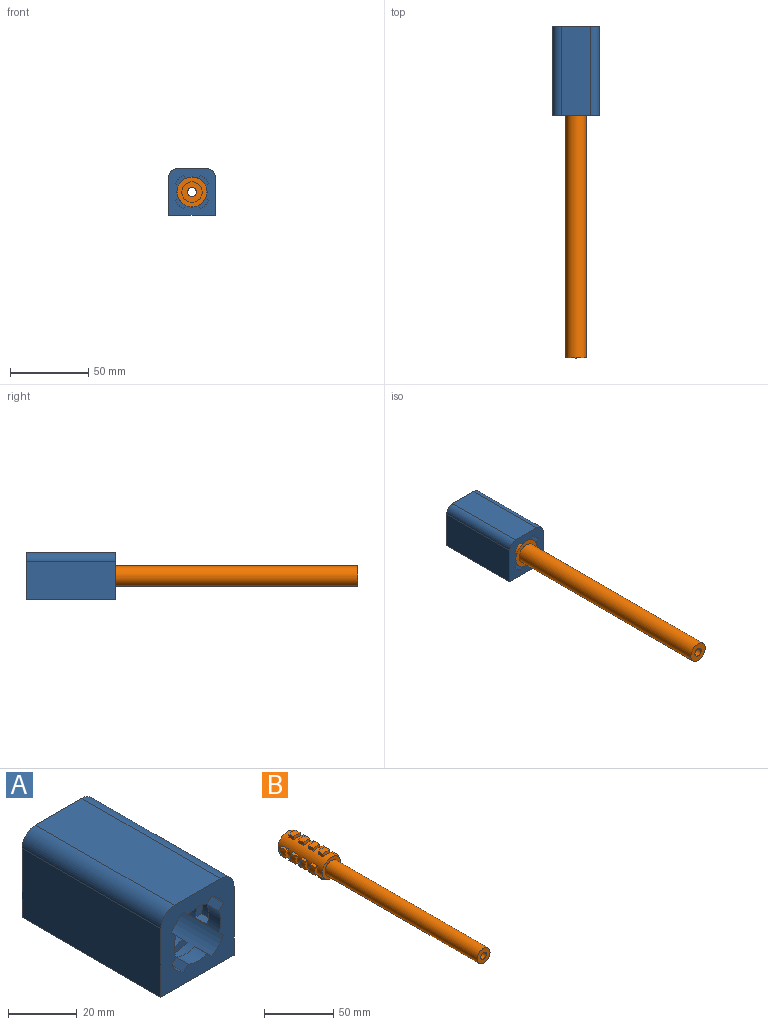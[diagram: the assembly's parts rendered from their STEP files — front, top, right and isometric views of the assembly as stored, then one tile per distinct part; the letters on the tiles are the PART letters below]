
ASSEMBLY  parts=2 mates=1
PART A: 121 faces, bbox 30x57x30 mm
  f0: plane 30x30mm, normal (0,1,0), area 631mm2, adj f33,f34,f35,f36,f37,f42,f43,f95
  f1: plane 4.88x4.88mm, normal (0,-1,0), area 12.5mm2, adj f37,f96,f109,f117
  f2: plane 5.27x3.17mm, normal (0,-1,0), area 12.5mm2, adj f37,f107,f110,f116
  f3: plane 4.88x4.88mm, normal (0,-1,0), area 12.5mm2, adj f37,f105,f108,f115
  f4: plane 5.27x3.17mm, normal (0,-1,0), area 12.5mm2, adj f37,f103,f106,f114
  f5: plane 4.88x4.88mm, normal (0,-1,0), area 12.5mm2, adj f37,f102,f104,f113
  f6: plane 5.27x3.17mm, normal (0,-1,0), area 12.5mm2, adj f37,f99,f101,f112
  f7: plane 4.88x4.88mm, normal (0,-1,0), area 12.5mm2, adj f37,f97,f100,f111
  f8: plane 5.27x3.17mm, normal (0,-1,0), area 12.5mm2, adj f37,f95,f98,f118
  f9: cylinder r=12.1mm len=40mm, axis (0,1,0), area 474.1mm2, adj f10,f17,f21,f25,f30,f47,f50,f60
  f10: plane 5x2.64mm, normal (0,0,-1), area 13.2mm2, adj f9,f37,f84,f93
  f11: cylinder r=12.1mm len=40mm, axis (0,1,0), area 474.1mm2, adj f12,f18,f22,f26,f31,f48,f50,f57
  f12: plane 5x2.64mm, normal (-1,0,0), area 13.2mm2, adj f11,f37,f81,f91
  f13: cylinder r=12.1mm len=40mm, axis (0,1,0), area 474.1mm2, adj f14,f19,f23,f27,f32,f49,f50,f54
  f14: plane 5x2.64mm, normal (0,0,1), area 13.2mm2, adj f13,f37,f79,f89
  f15: cylinder r=12.1mm len=40mm, axis (0,1,0), area 474.1mm2, adj f16,f20,f24,f28,f29,f46,f50,f51
  f16: plane 5x2.64mm, normal (1,0,0), area 13.2mm2, adj f15,f37,f75,f87
  f17: plane 5x2.64mm, normal (0,0,-1), area 13.2mm2, adj f9,f37,f72,f85
  f18: plane 5x2.64mm, normal (-1,0,0), area 13.2mm2, adj f11,f37,f69,f82
  f19: plane 5x2.64mm, normal (0,0,1), area 13.2mm2, adj f13,f37,f66,f80
  f20: plane 5x2.64mm, normal (1,0,0), area 13.2mm2, adj f15,f37,f63,f76
  f21: plane 5x2.64mm, normal (0,0,-1), area 13.2mm2, adj f9,f37,f60,f73
  f22: plane 5x2.64mm, normal (-1,0,0), area 13.2mm2, adj f11,f37,f57,f70
  f23: plane 5x2.64mm, normal (0,0,1), area 13.2mm2, adj f13,f37,f54,f67
  f24: plane 5x2.64mm, normal (1,0,0), area 13.2mm2, adj f15,f37,f52,f64
  f25: plane 5x2.64mm, normal (0,0,-1), area 13.2mm2, adj f9,f30,f37,f61
  f26: plane 5x2.64mm, normal (-1,0,0), area 13.2mm2, adj f11,f31,f37,f58
  f27: plane 5x2.64mm, normal (0,0,1), area 13.2mm2, adj f13,f32,f37,f55
  f28: plane 5x2.64mm, normal (1,0,0), area 13.2mm2, adj f15,f29,f37,f53
  f29: plane 14.17x8.25mm, normal (0,-1,0), area 39.1mm2, adj f15,f28,f37,f46
  f30: plane 14.17x8.25mm, normal (0,-1,0), area 39.1mm2, adj f9,f25,f37,f47
  f31: plane 14.17x8.25mm, normal (0,-1,0), area 39.1mm2, adj f11,f26,f37,f48
  f32: plane 14.17x8.25mm, normal (0,-1,0), area 39.1mm2, adj f13,f27,f37,f49
  f33: plane 57x24.5mm, normal (1,0,0), area 1396.5mm2, adj f0,f36,f50,f119
  f34: plane 57x19mm, normal (0,0,1), area 1083mm2, adj f0,f50,f119,f120
  f35: plane 57x24.5mm, normal (-1,0,0), area 1396.5mm2, adj f0,f36,f50,f120
  f36: plane 57x30mm, normal (0,0,-1), area 1710mm2, adj f0,f33,f35,f50
  f37: cylinder r=9.6mm len=57mm, axis (0,1,0), area 1300mm2, adj f0,f1,f2,f3,f4,f5,f6,f7
  f38: cylinder r=9.6mm len=6.48mm, axis (0,1,0), area 33.1mm2, adj f37,f57,f58,f59
  f39: cylinder r=9.6mm len=6.48mm, axis (0,1,0), area 33.1mm2, adj f37,f69,f70,f71
  f40: cylinder r=9.6mm len=6.48mm, axis (0,1,0), area 33.1mm2, adj f37,f81,f82,f83
  f41: cylinder r=9.6mm len=6.48mm, axis (0,1,0), area 33.1mm2, adj f37,f50,f91,f92
  f42: cylinder r=2.5mm len=12mm, axis (0,-1,0), area 188.5mm2, adj f0,f44
  f43: cylinder r=2.5mm len=12mm, axis (0,-1,0), area 188.5mm2, adj f0,f45
  f44: plane 5x5mm, normal (0,1,0), area 19.6mm2, adj f42
  f45: plane 5x5mm, normal (0,1,0), area 19.6mm2, adj f43
  f46: plane 40x1.87mm, normal (-0.71,0,-0.71), area 105.7mm2, adj f15,f29,f37,f50
  f47: plane 40x1.87mm, normal (-0.71,0,0.71), area 105.7mm2, adj f9,f30,f37,f50
  f48: plane 40x1.87mm, normal (0.71,0,0.71), area 105.7mm2, adj f11,f31,f37,f50
  f49: plane 40x1.87mm, normal (0.71,0,-0.71), area 105.7mm2, adj f13,f32,f37,f50
  f50: plane 30x30mm, normal (0,-1,0), area 526.2mm2, adj f9,f11,f13,f15,f33,f34,f35,f36
  f51: plane 5x1.87mm, normal (0.71,0,0.71), area 13.2mm2, adj f15,f37,f52,f53
  f52: plane 9.22x3.3mm, normal (0,-1,0), area 21.3mm2, adj f15,f24,f37,f51
  f53: plane 9.22x3.3mm, normal (0,1,0), area 21.3mm2, adj f15,f28,f37,f51
  f54: plane 9.22x3.3mm, normal (0,-1,0), area 21.3mm2, adj f13,f23,f37,f56
  f55: plane 9.22x3.3mm, normal (0,1,0), area 21.3mm2, adj f13,f27,f37,f56
  f56: plane 5x1.87mm, normal (-0.71,0,0.71), area 13.2mm2, adj f13,f37,f54,f55
  f57: plane 9.22x3.3mm, normal (0,-1,0), area 21.3mm2, adj f11,f22,f37,f38,f59
  f58: plane 9.22x3.3mm, normal (0,1,0), area 21.3mm2, adj f11,f26,f37,f38,f59
  f59: plane 5x1.87mm, normal (-0.71,0,-0.71), area 13.2mm2, adj f11,f38,f57,f58
  f60: plane 9.22x3.3mm, normal (0,-1,0), area 21.3mm2, adj f9,f21,f37,f62
  f61: plane 9.22x3.3mm, normal (0,1,0), area 21.3mm2, adj f9,f25,f37,f62
  f62: plane 5x1.87mm, normal (0.71,0,-0.71), area 13.2mm2, adj f9,f37,f60,f61
  f63: plane 9.22x3.3mm, normal (0,-1,0), area 21.3mm2, adj f15,f20,f37,f65
  f64: plane 9.22x3.3mm, normal (0,1,0), area 21.3mm2, adj f15,f24,f37,f65
  f65: plane 5x1.87mm, normal (0.71,0,0.71), area 13.2mm2, adj f15,f37,f63,f64
  f66: plane 9.22x3.3mm, normal (0,-1,0), area 21.3mm2, adj f13,f19,f37,f68
  f67: plane 9.22x3.3mm, normal (0,1,0), area 21.3mm2, adj f13,f23,f37,f68
  f68: plane 5x1.87mm, normal (-0.71,0,0.71), area 13.2mm2, adj f13,f37,f66,f67
  f69: plane 9.22x3.3mm, normal (0,-1,0), area 21.3mm2, adj f11,f18,f37,f39,f71
  f70: plane 9.22x3.3mm, normal (0,1,0), area 21.3mm2, adj f11,f22,f37,f39,f71
  f71: plane 5x1.87mm, normal (-0.71,0,-0.71), area 13.2mm2, adj f11,f39,f69,f70
  f72: plane 9.22x3.3mm, normal (0,-1,0), area 21.3mm2, adj f9,f17,f37,f74
  f73: plane 9.22x3.3mm, normal (0,1,0), area 21.3mm2, adj f9,f21,f37,f74
  f74: plane 5x1.87mm, normal (0.71,0,-0.71), area 13.2mm2, adj f9,f37,f72,f73
  f75: plane 9.22x3.3mm, normal (0,-1,0), area 21.3mm2, adj f15,f16,f37,f77
  f76: plane 9.22x3.3mm, normal (0,1,0), area 21.3mm2, adj f15,f20,f37,f77
  f77: plane 5x1.87mm, normal (0.71,0,0.71), area 13.2mm2, adj f15,f37,f75,f76
  f78: plane 5x1.87mm, normal (-0.71,0,0.71), area 13.2mm2, adj f13,f37,f79,f80
  f79: plane 9.22x3.3mm, normal (0,-1,0), area 21.3mm2, adj f13,f14,f37,f78
  f80: plane 9.22x3.3mm, normal (0,1,0), area 21.3mm2, adj f13,f19,f37,f78
  f81: plane 9.22x3.3mm, normal (0,-1,0), area 21.3mm2, adj f11,f12,f37,f40,f83
  f82: plane 9.22x3.3mm, normal (0,1,0), area 21.3mm2, adj f11,f18,f37,f40,f83
  f83: plane 5x1.87mm, normal (-0.71,0,-0.71), area 13.2mm2, adj f11,f40,f81,f82
  f84: plane 9.22x3.3mm, normal (0,-1,0), area 21.3mm2, adj f9,f10,f37,f86
  f85: plane 9.22x3.3mm, normal (0,1,0), area 21.3mm2, adj f9,f17,f37,f86
  f86: plane 5x1.87mm, normal (0.71,0,-0.71), area 13.2mm2, adj f9,f37,f84,f85
  f87: plane 9.22x3.3mm, normal (0,1,0), area 21.3mm2, adj f15,f16,f37,f88
  f88: plane 5x1.87mm, normal (0.71,0,0.71), area 13.2mm2, adj f15,f37,f50,f87
  f89: plane 9.22x3.3mm, normal (0,1,0), area 21.3mm2, adj f13,f14,f37,f90
  f90: plane 5x1.87mm, normal (-0.71,0,0.71), area 13.2mm2, adj f13,f37,f50,f89
  f91: plane 9.22x3.3mm, normal (0,1,0), area 21.3mm2, adj f11,f12,f37,f41,f92
  f92: plane 5x1.87mm, normal (-0.71,0,-0.71), area 13.2mm2, adj f11,f41,f50,f91
  f93: plane 9.22x3.3mm, normal (0,1,0), area 21.3mm2, adj f9,f10,f37,f94
  f94: plane 5x1.87mm, normal (0.71,0,-0.71), area 13.2mm2, adj f9,f37,f50,f93
  f95: plane 6.01x2.81mm, normal (0.92,0,-0.38), area 15.1mm2, adj f0,f8,f37,f118
  f96: plane 6.01x2.81mm, normal (-0.92,0,0.38), area 15.1mm2, adj f0,f1,f37,f117
  f97: plane 6.01x2.81mm, normal (0.92,0,0.38), area 15.1mm2, adj f0,f7,f37,f111
  f98: plane 6.01x2.81mm, normal (-0.92,0,-0.38), area 15.1mm2, adj f0,f8,f37,f118
  f99: plane 6.01x2.81mm, normal (0.38,0,0.92), area 15.1mm2, adj f0,f6,f37,f112
  f100: plane 6.01x2.81mm, normal (-0.38,0,-0.92), area 15.1mm2, adj f0,f7,f37,f111
  f101: plane 6.01x2.81mm, normal (0.38,0,-0.92), area 15.1mm2, adj f0,f6,f37,f112
  f102: plane 6.01x2.81mm, normal (-0.38,0,0.92), area 15.1mm2, adj f0,f5,f37,f113
  f103: plane 6.01x2.81mm, normal (-0.92,0,0.38), area 15.1mm2, adj f0,f4,f37,f114
  f104: plane 6.01x2.81mm, normal (0.92,0,-0.38), area 15.1mm2, adj f0,f5,f37,f113
  f105: plane 6.01x2.81mm, normal (-0.92,0,-0.38), area 15.1mm2, adj f0,f3,f37,f115
  f106: plane 6.01x2.81mm, normal (0.92,0,0.38), area 15.1mm2, adj f0,f4,f37,f114
  f107: plane 6.01x2.81mm, normal (-0.38,0,-0.92), area 15.1mm2, adj f0,f2,f37,f116
  f108: plane 6.01x2.81mm, normal (0.38,0,0.92), area 15.1mm2, adj f0,f3,f37,f115
  f109: plane 6.01x2.81mm, normal (0.38,0,-0.92), area 15.1mm2, adj f0,f1,f37,f117
  f110: plane 6.01x2.81mm, normal (-0.38,0,0.92), area 15.1mm2, adj f0,f2,f37,f116
  f111: cone r=7.6mm half-angle=9.5deg, axis (0,1,0), area 20.4mm2, adj f0,f7,f97,f100
  f112: cone r=7.6mm half-angle=9.5deg, axis (0,1,0), area 20.4mm2, adj f0,f6,f99,f101
  f113: cone r=7.6mm half-angle=9.5deg, axis (0,1,0), area 20.4mm2, adj f0,f5,f102,f104
  f114: cone r=7.6mm half-angle=9.5deg, axis (0,1,0), area 20.4mm2, adj f0,f4,f103,f106
  f115: cone r=7.6mm half-angle=9.5deg, axis (0,1,0), area 20.4mm2, adj f0,f3,f105,f108
  f116: cone r=7.6mm half-angle=9.5deg, axis (0,1,0), area 20.4mm2, adj f0,f2,f107,f110
  f117: cone r=7.6mm half-angle=9.5deg, axis (0,1,0), area 20.4mm2, adj f0,f1,f96,f109
  f118: cone r=7.6mm half-angle=9.5deg, axis (0,1,0), area 20.4mm2, adj f0,f8,f95,f98
  f119: cylinder r=5.5mm len=57mm, axis (0,-1,0), area 492.4mm2, adj f0,f33,f34,f50
  f120: cylinder r=5.5mm len=57mm, axis (0,1,0), area 492.4mm2, adj f0,f34,f35,f50
PART B: 107 faces, bbox 24x200x24 mm
  f0: plane 5x2.65mm, normal (-1,0,0), area 13.2mm2, adj f2,f3,f68,f89
  f1: plane 4.5x2.65mm, normal (1,0,0), area 11.9mm2, adj f2,f68,f89,f106
  f2: plane 7x3.17mm, normal (0,1,0), area 17.8mm2, adj f0,f1,f68,f89
  f3: plane 6.5x3.17mm, normal (0,-1,0), area 16.5mm2, adj f0,f68,f89,f106
  f4: plane 5x2.65mm, normal (-1,0,0), area 13.2mm2, adj f6,f7,f68,f88
  f5: plane 4.5x2.65mm, normal (1,0,0), area 11.9mm2, adj f6,f68,f88,f105
  f6: plane 7x3.17mm, normal (0,1,0), area 17.8mm2, adj f4,f5,f68,f88
  f7: plane 6.5x3.17mm, normal (0,-1,0), area 16.5mm2, adj f4,f68,f88,f105
  f8: plane 5x2.65mm, normal (-1,0,0), area 13.2mm2, adj f10,f11,f68,f87
  f9: plane 4.5x2.65mm, normal (1,0,0), area 11.9mm2, adj f10,f68,f87,f104
  f10: plane 7x3.17mm, normal (0,1,0), area 17.8mm2, adj f8,f9,f68,f87
  f11: plane 6.5x3.17mm, normal (0,-1,0), area 16.5mm2, adj f8,f68,f87,f104
  f12: plane 5x2.65mm, normal (-1,0,0), area 13.2mm2, adj f14,f15,f68,f86
  f13: plane 4.5x2.65mm, normal (1,0,0), area 11.9mm2, adj f14,f68,f86,f103
  f14: plane 7x3.17mm, normal (0,1,0), area 17.8mm2, adj f12,f13,f68,f86
  f15: plane 6.5x3.17mm, normal (0,-1,0), area 16.5mm2, adj f12,f68,f86,f103
  f16: plane 5x2.65mm, normal (0,0,1), area 13.2mm2, adj f18,f19,f68,f85
  f17: plane 4.5x2.65mm, normal (0,0,-1), area 11.9mm2, adj f18,f68,f85,f102
  f18: plane 7x3.17mm, normal (0,1,0), area 17.8mm2, adj f16,f17,f68,f85
  f19: plane 6.5x3.17mm, normal (0,-1,0), area 16.5mm2, adj f16,f68,f85,f102
  f20: plane 5x2.65mm, normal (0,0,1), area 13.2mm2, adj f22,f23,f68,f84
  f21: plane 4.5x2.65mm, normal (0,0,-1), area 11.9mm2, adj f22,f68,f84,f101
  f22: plane 7x3.17mm, normal (0,1,0), area 17.8mm2, adj f20,f21,f68,f84
  f23: plane 6.5x3.17mm, normal (0,-1,0), area 16.5mm2, adj f20,f68,f84,f101
  f24: plane 5x2.65mm, normal (0,0,1), area 13.2mm2, adj f26,f27,f68,f83
  f25: plane 4.5x2.65mm, normal (0,0,-1), area 11.9mm2, adj f26,f68,f83,f100
  f26: plane 7x3.17mm, normal (0,1,0), area 17.8mm2, adj f24,f25,f68,f83
  f27: plane 6.5x3.17mm, normal (0,-1,0), area 16.5mm2, adj f24,f68,f83,f100
  f28: plane 5x2.65mm, normal (0,0,1), area 13.2mm2, adj f30,f31,f68,f82
  f29: plane 4.5x2.65mm, normal (0,0,-1), area 11.9mm2, adj f30,f68,f82,f99
  f30: plane 7x3.17mm, normal (0,1,0), area 17.8mm2, adj f28,f29,f68,f82
  f31: plane 6.5x3.17mm, normal (0,-1,0), area 16.5mm2, adj f28,f68,f82,f99
  f32: plane 5x2.65mm, normal (1,0,0), area 13.2mm2, adj f34,f35,f68,f81
  f33: plane 4.5x2.65mm, normal (-1,0,0), area 11.9mm2, adj f34,f68,f81,f98
  f34: plane 7x3.17mm, normal (0,1,0), area 17.8mm2, adj f32,f33,f68,f81
  f35: plane 6.5x3.17mm, normal (0,-1,0), area 16.5mm2, adj f32,f68,f81,f98
  f36: plane 5x2.65mm, normal (1,0,0), area 13.2mm2, adj f38,f39,f68,f80
  f37: plane 4.5x2.65mm, normal (-1,0,0), area 11.9mm2, adj f38,f68,f80,f97
  f38: plane 7x3.17mm, normal (0,1,0), area 17.8mm2, adj f36,f37,f68,f80
  f39: plane 6.5x3.17mm, normal (0,-1,0), area 16.5mm2, adj f36,f68,f80,f97
  f40: plane 5x2.65mm, normal (1,0,0), area 13.2mm2, adj f42,f43,f68,f79
  f41: plane 4.5x2.65mm, normal (-1,0,0), area 11.9mm2, adj f42,f68,f79,f96
  f42: plane 7x3.17mm, normal (0,1,0), area 17.8mm2, adj f40,f41,f68,f79
  f43: plane 6.5x3.17mm, normal (0,-1,0), area 16.5mm2, adj f40,f68,f79,f96
  f44: plane 5x2.65mm, normal (1,0,0), area 13.2mm2, adj f46,f47,f68,f78
  f45: plane 4.5x2.65mm, normal (-1,0,0), area 11.9mm2, adj f46,f68,f78,f95
  f46: plane 7x3.17mm, normal (0,1,0), area 17.8mm2, adj f44,f45,f68,f78
  f47: plane 6.5x3.17mm, normal (0,-1,0), area 16.5mm2, adj f44,f68,f78,f95
  f48: plane 5x2.65mm, normal (0,0,-1), area 13.2mm2, adj f50,f51,f68,f77
  f49: plane 4.5x2.65mm, normal (0,0,1), area 11.9mm2, adj f50,f68,f77,f94
  f50: plane 7x3.17mm, normal (0,1,0), area 17.8mm2, adj f48,f49,f68,f77
  f51: plane 6.5x3.17mm, normal (0,-1,0), area 16.5mm2, adj f48,f68,f77,f94
  f52: plane 5x2.65mm, normal (0,0,-1), area 13.2mm2, adj f54,f55,f68,f76
  f53: plane 4.5x2.65mm, normal (0,0,1), area 11.9mm2, adj f54,f68,f76,f93
  f54: plane 7x3.17mm, normal (0,1,0), area 17.8mm2, adj f52,f53,f68,f76
  f55: plane 6.5x3.17mm, normal (0,-1,0), area 16.5mm2, adj f52,f68,f76,f93
  f56: plane 5x2.65mm, normal (0,0,-1), area 13.2mm2, adj f58,f59,f68,f75
  f57: plane 4.5x2.65mm, normal (0,0,1), area 11.9mm2, adj f58,f68,f75,f92
  f58: plane 7x3.17mm, normal (0,1,0), area 17.8mm2, adj f56,f57,f68,f75
  f59: plane 6.5x3.17mm, normal (0,-1,0), area 16.5mm2, adj f56,f68,f75,f92
  f60: plane 5x2.65mm, normal (0,0,-1), area 13.2mm2, adj f62,f63,f68,f74
  f61: plane 4.5x2.65mm, normal (0,0,1), area 11.9mm2, adj f62,f68,f74,f91
  f62: plane 7x3.17mm, normal (0,1,0), area 17.8mm2, adj f60,f61,f68,f74
  f63: plane 6.5x3.17mm, normal (0,-1,0), area 16.5mm2, adj f60,f68,f74,f91
  f64: cylinder r=3.21mm len=6.43mm, axis (0,1,0), area 104mm2, adj f65,f73
  f65: cone r=4.5mm half-angle=23deg, axis (0,1,0), area 79.8mm2, adj f64,f66
  f66: cone r=4.79mm half-angle=0.5deg, axis (0,1,0), area 974.5mm2, adj f65,f90
  f67: plane 19x19mm, normal (0,1,0), area 169.7mm2, adj f68,f90
  f68: cylinder r=9.5mm len=45mm, axis (0,1,0), area 2114.7mm2, adj f0,f1,f2,f3,f4,f5,f6,f7
  f69: plane 19x19mm, normal (0,-1,0), area 150.8mm2, adj f68,f70
  f70: cylinder r=6.5mm len=155mm, axis (0,1,0), area 6330.3mm2, adj f69,f71
  f71: plane 13x13mm, normal (0,-1,0), area 107.2mm2, adj f70,f72
  f72: cylinder r=2.85mm len=157.2mm, axis (0,1,0), area 2815mm2, adj f71,f73
  f73: plane 6.43x6.43mm, normal (0,1,0), area 7mm2, adj f64,f72
  f74: cylinder r=12mm len=7mm, axis (0,1,0), area 35.4mm2, adj f60,f61,f62,f63,f91
  f75: cylinder r=12mm len=7mm, axis (0,1,0), area 35.4mm2, adj f56,f57,f58,f59,f92
  f76: cylinder r=12mm len=7mm, axis (0,1,0), area 35.4mm2, adj f52,f53,f54,f55,f93
  f77: cylinder r=12mm len=7mm, axis (0,1,0), area 35.4mm2, adj f48,f49,f50,f51,f94
  f78: cylinder r=12mm len=7mm, axis (0,1,0), area 35.4mm2, adj f44,f45,f46,f47,f95
  f79: cylinder r=12mm len=7mm, axis (0,1,0), area 35.4mm2, adj f40,f41,f42,f43,f96
  f80: cylinder r=12mm len=7mm, axis (0,1,0), area 35.4mm2, adj f36,f37,f38,f39,f97
  f81: cylinder r=12mm len=7mm, axis (0,1,0), area 35.4mm2, adj f32,f33,f34,f35,f98
  f82: cylinder r=12mm len=7mm, axis (0,1,0), area 35.4mm2, adj f28,f29,f30,f31,f99
  f83: cylinder r=12mm len=7mm, axis (0,1,0), area 35.4mm2, adj f24,f25,f26,f27,f100
  f84: cylinder r=12mm len=7mm, axis (0,1,0), area 35.4mm2, adj f20,f21,f22,f23,f101
  f85: cylinder r=12mm len=7mm, axis (0,1,0), area 35.4mm2, adj f16,f17,f18,f19,f102
  f86: cylinder r=12mm len=7mm, axis (0,1,0), area 35.4mm2, adj f12,f13,f14,f15,f103
  f87: cylinder r=12mm len=7mm, axis (0,1,0), area 35.4mm2, adj f8,f9,f10,f11,f104
  f88: cylinder r=12mm len=7mm, axis (0,1,0), area 35.4mm2, adj f4,f5,f6,f7,f105
  f89: cylinder r=12mm len=7mm, axis (0,1,0), area 35.4mm2, adj f0,f1,f2,f3,f106
  f90: cone r=4.79mm half-angle=45deg, axis (0,1,0), area 59.1mm2, adj f66,f67
  f91: plane 2.79x0.5mm, normal (0,-0.71,0.71), area 1.9mm2, adj f61,f63,f68,f74
  f92: plane 2.79x0.5mm, normal (0,-0.71,0.71), area 1.9mm2, adj f57,f59,f68,f75
  f93: plane 2.79x0.5mm, normal (0,-0.71,0.71), area 1.9mm2, adj f53,f55,f68,f76
  f94: plane 2.79x0.5mm, normal (0,-0.71,0.71), area 1.9mm2, adj f49,f51,f68,f77
  f95: plane 2.79x0.5mm, normal (-0.71,-0.71,0), area 1.9mm2, adj f45,f47,f68,f78
  f96: plane 2.79x0.5mm, normal (-0.71,-0.71,0), area 1.9mm2, adj f41,f43,f68,f79
  f97: plane 2.79x0.5mm, normal (-0.71,-0.71,0), area 1.9mm2, adj f37,f39,f68,f80
  f98: plane 2.79x0.5mm, normal (-0.71,-0.71,0), area 1.9mm2, adj f33,f35,f68,f81
  f99: plane 2.79x0.5mm, normal (0,-0.71,-0.71), area 1.9mm2, adj f29,f31,f68,f82
  f100: plane 2.79x0.5mm, normal (0,-0.71,-0.71), area 1.9mm2, adj f25,f27,f68,f83
  f101: plane 2.79x0.5mm, normal (0,-0.71,-0.71), area 1.9mm2, adj f21,f23,f68,f84
  f102: plane 2.79x0.5mm, normal (0,-0.71,-0.71), area 1.9mm2, adj f17,f19,f68,f85
  f103: plane 2.79x0.5mm, normal (0.71,-0.71,0), area 1.9mm2, adj f13,f15,f68,f86
  f104: plane 2.79x0.5mm, normal (0.71,-0.71,0), area 1.9mm2, adj f9,f11,f68,f87
  f105: plane 2.79x0.5mm, normal (0.71,-0.71,0), area 1.9mm2, adj f5,f7,f68,f88
  f106: plane 2.79x0.5mm, normal (0.71,-0.71,0), area 1.9mm2, adj f1,f3,f68,f89
PLACE A t=(0.06,16.45,-0.14)mm fixed
PLACE B t=(0.06,16.45,-0.14)mm
MATE cylindrical B.f64 <-> A.f37  axis (0,1,0) through (0.06,11.45,-0.14)mm
